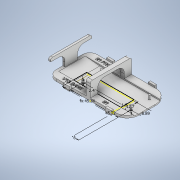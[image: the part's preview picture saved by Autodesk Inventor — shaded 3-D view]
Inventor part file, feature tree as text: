
AUTODESK INVENTOR PART (.ipt)
format: ipt  version: 2021 (Build 250183000, 183)  size: 1,772,032 bytes
history: native  units: in
note: dims shown in document units (in); Inventor stores cm internally (conversion verified against a paired STEP export)
features: extrude x12, sketch x11, fillet x6, mirror x3, plane x2, chamfer x1
ambient origin geometry x8: Origin, YZ Plane, XZ Plane, XY Plane, X Axis, Y Axis, Z Axis, Center Point
bodies: Solid1 (feature_tree)
feature tree (35):
  extrude  "Extrusion1"  Depth=0.7756in
  extrude  "Extrusion2"  Depth=0.2362in
  plane  "Work Plane1"
  extrude  "Extrusion3"  Depth=0.2362in
  sketch  "Sketch5"  dims[d14=1.3386in d15=0.0in]
  extrude  "Extrusion4"  TaperAngle=0.0deg  [1 undecoded]
  sketch  "Sketch7"  dims[d19=0.8661in d20=0.5512in d21=0.0in d22=0.7756in]
  extrude  "Extrusion5"  Depth=0.1575in
  plane  "Work Plane2"
  extrude  "Extrusion8"  Depth=0.5512in
  fillet  "Fillet3"  [1 undecoded]
  fillet  "Fillet4"  Radius=0.7756in
  sketch  "Sketch13"  dims[d26=1.4803in]
  extrude  "Extrusion9"  Depth=0.5in
  mirror  "Mirror3"
  chamfer  "Chamfer1"  Distance=0.748in
  extrude  "Extrusion11"  Depth=0.5in
  extrude  "Extrusion13"  Depth=0.0472in TaperAngle=0.0deg
  mirror  "Mirror4"
  extrude  "Extrusion14"  Depth=0.0787in
  extrude  "Extrusion15"  Depth=0.2756in
  mirror  "Mirror5"
  fillet  "Fillet8"  Radius=0.0709in
  fillet  "Fillet9"  Radius=0.0945in
  fillet  "Fillet10"  Radius=1.8in
  extrude  "Extrusion17"  Depth=0.35in
  fillet  "Fillet11"  Radius=0.1575in
  sketch  "Sketch1"  dims[d5=2.4409in d6=0.7756in]
  sketch  "Sketch3"  dims[d7=0.0945in d8=0.0in d9=0.2362in]
  sketch  "Sketch4"  dims[d10=0.0787in d11=0.0in d13=0.2362in]
  sketch  "Sketch6"  dims[d16=0.063in d17=0.0in d18=0.1575in]
  sketch  "Sketch8"  dims[d23=0.5512in d24=0.5in]
  sketch  "Sketch12"  dims[d25=0.4331in]
  sketch  "Sketch18"  dims[d27=0.0in d29=-0.748in d30=0.748in]
  sketch  "Sketch19"  dims[d41=1.785in d42=0.5in d43=0.0472in d44=0.0in d46=0.0787in d47=0.2756in d48=0.0709in d49=0.0945in d50=1.8in d51=0.35in d52=0.1575in d53=0.0in d56=0.5512in d57=0.0472in d58=45.0deg d59=0.0787in d60=0.0787in d61=0.0394in d64=0.0394in d66=0.0787in d67=0.0394in d68=0.0in d69=0.0in d70=0.0in d71=0.2397in d72=0.2397in d74=0.315in d76=0.2362in d77=0.0787in d78=0.0in d79=0.0945in d84=0.4331in d85=0.0in d86=0.0in d87=0.0787in d90=0.0787in d91=0.7756in d92=0.1181in d93=0.0in d96=0.0in d97=0.2362in d98=0.2756in d99=0.0787in d100=0.0in d101=0.315in d104=0.0472in d105=0.0472in d106=0.5118in d107=0.0in d108=0.5118in d102=0.0197in d103=0.0344in]
note: 2 required parameter values undecoded (feature->parameter linkage not recoverable at this tier; creation-order binding heuristic only, values carry confidence <= 0.55)
